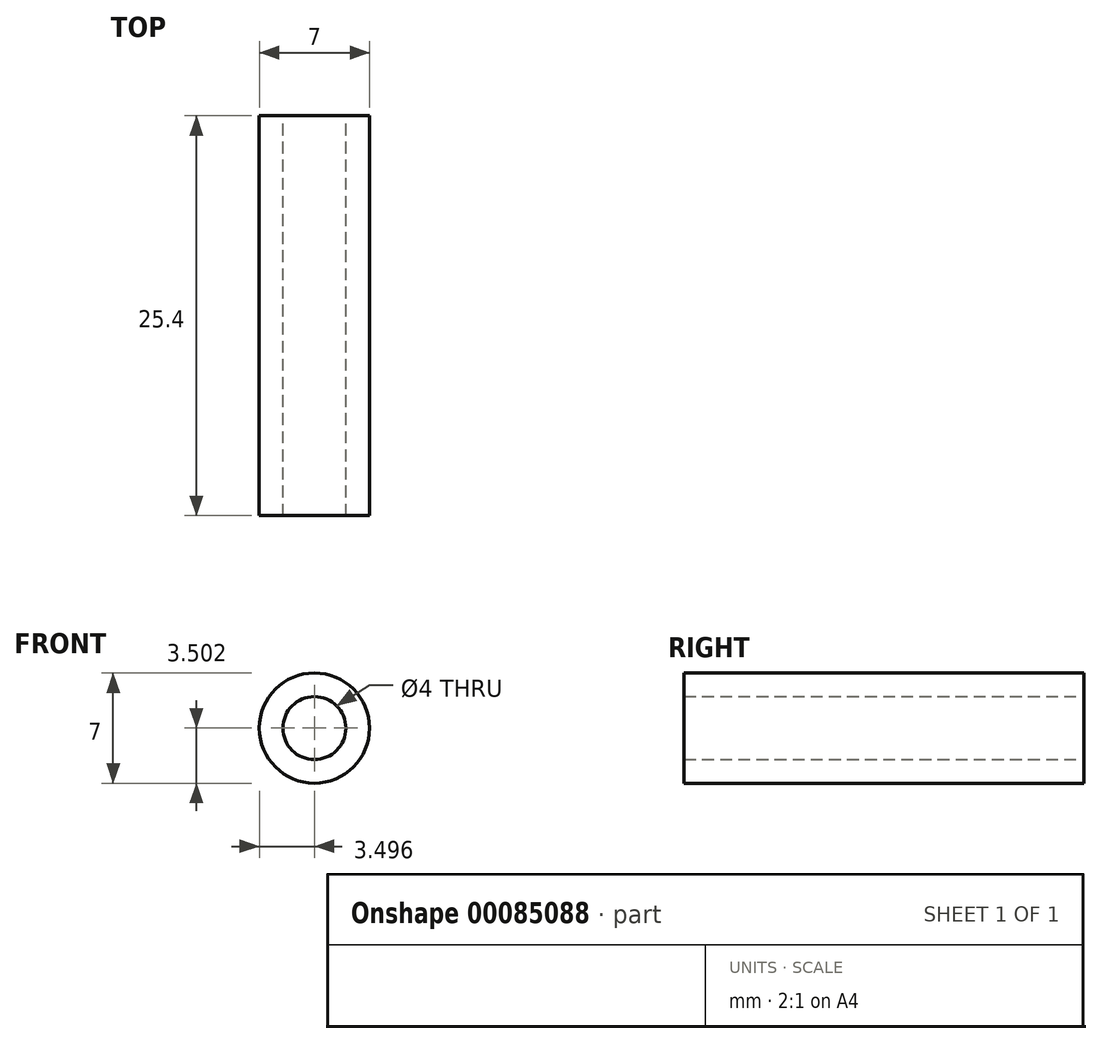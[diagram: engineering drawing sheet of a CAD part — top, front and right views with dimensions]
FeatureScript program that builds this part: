
annotation { "Feature Type Name" : "Feature", "Feature Type Description" : "" }
export const myFeature = defineFeature(function(context is Context, id is Id, definition is map)
    precondition{}
    {
        {
            var Q0;
            Q0=qCreatedBy(makeId("Front.planeOp"),FACE);
            var sketch = newSketch(context, id + "F0", { "sketchPlane" : qUnion([Q0])});
            skCircle(sketch, "E0", {"center": v(-3.47, 10.08) * mm, "radius": 3.5 * mm});
            skCircle(sketch, "E1", {"center": v(-3.47, 10.08) * mm, "radius": 2 * mm});
            skSolve(sketch);
        }
        {
            var Q0;
            Q0 = qSketchRegion(id + "F0", true);
            extrude(context, id + "F1", {"entities" : qUnion([Q0]), "depth" : 25.4 * mm});
        }
    });
